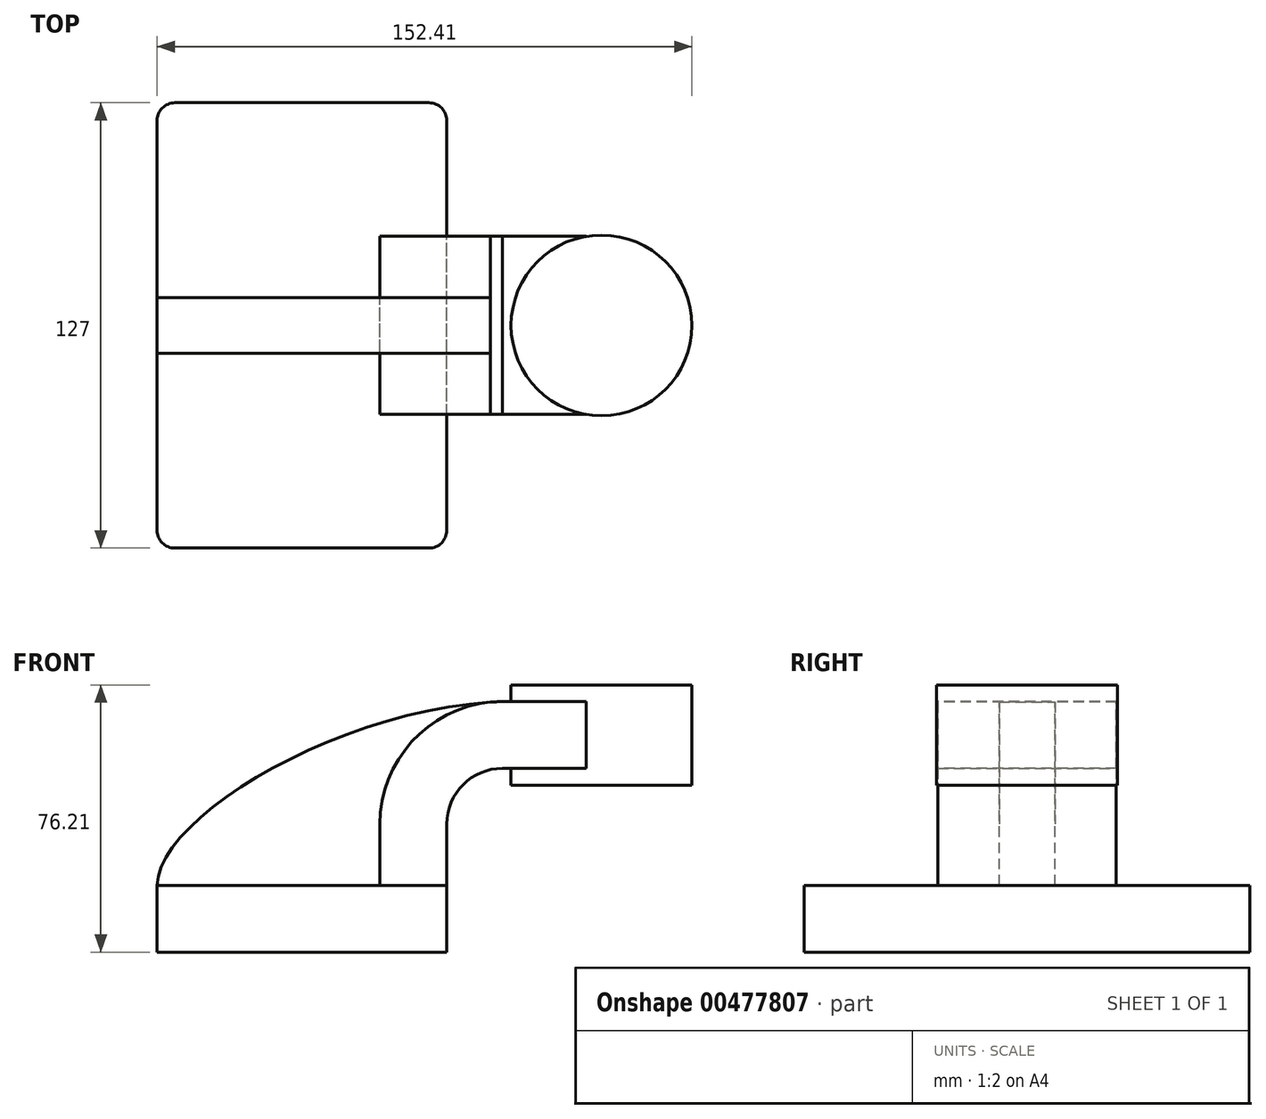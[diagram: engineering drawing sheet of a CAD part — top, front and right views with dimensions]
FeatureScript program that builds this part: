
annotation { "Feature Type Name" : "Feature", "Feature Type Description" : "" }
export const myFeature = defineFeature(function(context is Context, id is Id, definition is map)
    precondition{}
    {
        {
            var Q0;
            Q0=qCreatedBy(makeId("Front.planeOp"),FACE);
            var sketch = newSketch(context, id + "F0", { "sketchPlane" : qUnion([Q0])});
            skLineSegment(sketch, "E0.bottom", {"start": v(-41.28, 9.52) * mm, "end": v(41.27, 9.53) * mm});
            skLineSegment(sketch, "E0.top", {"start": v(-41.27, -9.53) * mm, "end": v(41.28, -9.53) * mm});
            skLineSegment(sketch, "E0.left", {"start": v(-41.28, 9.52) * mm, "end": v(-41.28, -9.53) * mm});
            skLineSegment(sketch, "E0.right", {"start": v(41.28, 9.53) * mm, "end": v(41.28, -9.52) * mm});
            skPoint(sketch, "E0.middle", {"position": v(0, 0) * mm});
            skLineSegment(sketch, "E1.bottom", {"start": v(111.12, 66.67) * mm, "end": v(60.32, 66.67) * mm});
            skLineSegment(sketch, "E1.top", {"start": v(111.12, 38.1) * mm, "end": v(60.32, 38.1) * mm});
            skLineSegment(sketch, "E1.left", {"start": v(111.12, 66.68) * mm, "end": v(111.12, 38.1) * mm});
            skLineSegment(sketch, "E1.right", {"start": v(60.32, 66.68) * mm, "end": v(60.32, 38.1) * mm});
            skPoint(sketch, "E1.middle", {"position": v(85.72, 52.39) * mm});
            skLineSegment(sketch, "E2", {"start": v(41.27, 9.53) * mm, "end": v(41.27, 27) * mm});
            skArc(sketch, "E3", {"start": v(41.27, 27) * mm, "mid": v(45.92, 38.23) * mm, "end": v(57.15, 42.88) * mm});
            skLineSegment(sketch, "E4", {"start": v(57.15, 42.88) * mm, "end": v(85.36, 42.88) * mm});
            skLineSegment(sketch, "E5.0", {"start": v(57.15, 61.93) * mm, "end": v(85.36, 61.93) * mm});
            skArc(sketch, "E5.1", {"start": v(22.23, 27) * mm, "mid": v(32.45, 51.7) * mm, "end": v(57.15, 61.93) * mm});
            skLineSegment(sketch, "E5.2", {"start": v(22.23, 9.53) * mm, "end": v(22.23, 27) * mm});
            skFitSpline(sketch, "E6", {"points": [v(-41.28, 9.52) * mm, v(57.15, 61.93) * mm], "startDerivative": vector(0.63, 58.6) * mm, "endDerivative": vector(137.81, 4.67) * mm});
            skLineSegment(sketch, "E7", {"start": v(85.36, 66.67) * mm, "end": v(85.36, 38.1) * mm});
            skSolve(sketch);
        }
        {
            var Q0;
            Q0=makeQuery(id+"F0.imprint","IMPRINT",FACE,{"disambiguationData":[TD([[makeQuery(id+"F0.imprint","IMPRINT",EDGE,{"derivedFrom":sQuery(id+"F0.wireOp",EDGE,"E0.top")}),1.0]])]});
            extrude(context, id + "F1", {"entities" : qUnion([Q0]), "endBound" : BoundingType.SYMMETRIC, "depth" : 127 * mm, "hasSecondDirection" : true, "secondDirectionOppositeDirection" : true, "secondDirectionDepth" : 76.2 * mm});
        }
        {
            var Q0;
            {var subQ1=sQuery(id+"F0.wireOp",EDGE,"E2");Q0=makeQuery(id+"F0.imprint","IMPRINT",FACE,{"disambiguationData":[TD([[makeQuery(id+"F0.imprint","IMPRINT",EDGE,{"derivedFrom":subQ1}),1.0]])]});}
            var Q1;
            {var subQ0=sQuery(id+"F0.wireOp",EDGE,"E5.0");var subQ1=sQuery(id+"F0.wireOp",EDGE,"E1.right");var subQ2=makeQuery(id+"F0.imprint","INTERSECT",VERTEX,{"derivedFrom":[subQ1,subQ0]});Q1=makeQuery(id+"F0.imprint","IMPRINT",FACE,{"disambiguationData":[TD([[makeQuery(id+"F0.imprint","IMPRINT",EDGE,{"disambiguationData":[TD([[subQ2,-1.0]])],"derivedFrom":subQ1}),1.0]])]});}
            extrude(context, id + "F2", {"entities" : qUnion([Q0, Q1]), "endBound" : BoundingType.SYMMETRIC, "depth" : 50.8 * mm});
        }
        {
            var Q0;
            {var subQ3=sQuery(id+"F0.wireOp",EDGE,"E5.2");Q0=makeQuery(id+"F0.imprint","IMPRINT",FACE,{"disambiguationData":[TD([[makeQuery(id+"F0.imprint","IMPRINT",EDGE,{"derivedFrom":subQ3}),1.0]])]});}
            extrude(context, id + "F3", {"entities" : qUnion([Q0]), "endBound" : BoundingType.SYMMETRIC, "depth" : 15.88 * mm});
        }
        {
            var Q0;
            Q0=makeQuery(id+"F1.opExtrude","CAP_EDGE",EDGE,{"disambiguationData":[OSD([sQuery(id+"F0.wireOp",EDGE,"E0.left")])],"isStart":false});
            var Q1;
            Q1=makeQuery(id+"F1.opExtrude","CAP_EDGE",EDGE,{"disambiguationData":[OSD([sQuery(id+"F0.wireOp",EDGE,"E0.right")])],"isStart":false});
            var Q2;
            Q2=makeQuery(id+"F1.opExtrude","CAP_EDGE",EDGE,{"disambiguationData":[OSD([sQuery(id+"F0.wireOp",EDGE,"E0.left")])],"isStart":true});
            var Q3;
            Q3=makeQuery(id+"F1.opExtrude","CAP_EDGE",EDGE,{"disambiguationData":[OSD([sQuery(id+"F0.wireOp",EDGE,"E0.right")])],"isStart":true});
            fillet(context, id + "F4", {"entities" : qUnion([Q0, Q1, Q2, Q3]), "radius" : 5.08 * mm, "tangentPropagation" : true, "allowEdgeOverflow" : false});
        }
        {
            var Q0;
            {var subQ4=sQuery(id+"F0.wireOp",EDGE,"E1.left");Q0=makeQuery(id+"F0.imprint","IMPRINT",FACE,{"disambiguationData":[TD([[makeQuery(id+"F0.imprint","IMPRINT",EDGE,{"derivedFrom":subQ4}),-1.0]])]});}
            var Q1;
            Q1=sQuery(id+"F0.wireOp",EDGE,"E7");
            revolve(context, id + "F5", {"operationType" : NewBodyOperationType.ADD, "entities" : qUnion([Q0]), "axis" : qUnion([Q1]), "revolveType" : RevolveType.FULL});
        }
    });
